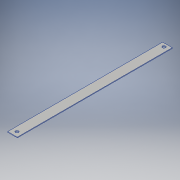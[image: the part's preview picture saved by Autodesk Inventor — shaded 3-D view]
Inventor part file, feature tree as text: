
AUTODESK INVENTOR PART (.ipt)
format: ipt  version: 2019 (Build 230136000, 136)  size: 105,472 bytes
history: native  units: mm
features: sketch x2, extrude x1, hole x1
ambient origin geometry x8: Origin, YZ Plane, XZ Plane, XY Plane, X Axis, Y Axis, Z Axis, Center Point
bodies: Solide1 (feature_tree)
feature tree (4):
  extrude  "Extrusion1"  Depth=226.0mm
  hole  "Perçage1"  [1 undecoded]
  sketch  "Esquisse2"
  sketch  "Esquisse3"
note: 1 required parameter value undecoded (feature->parameter linkage not recoverable at this tier; creation-order binding heuristic only, values carry confidence <= 0.55)
